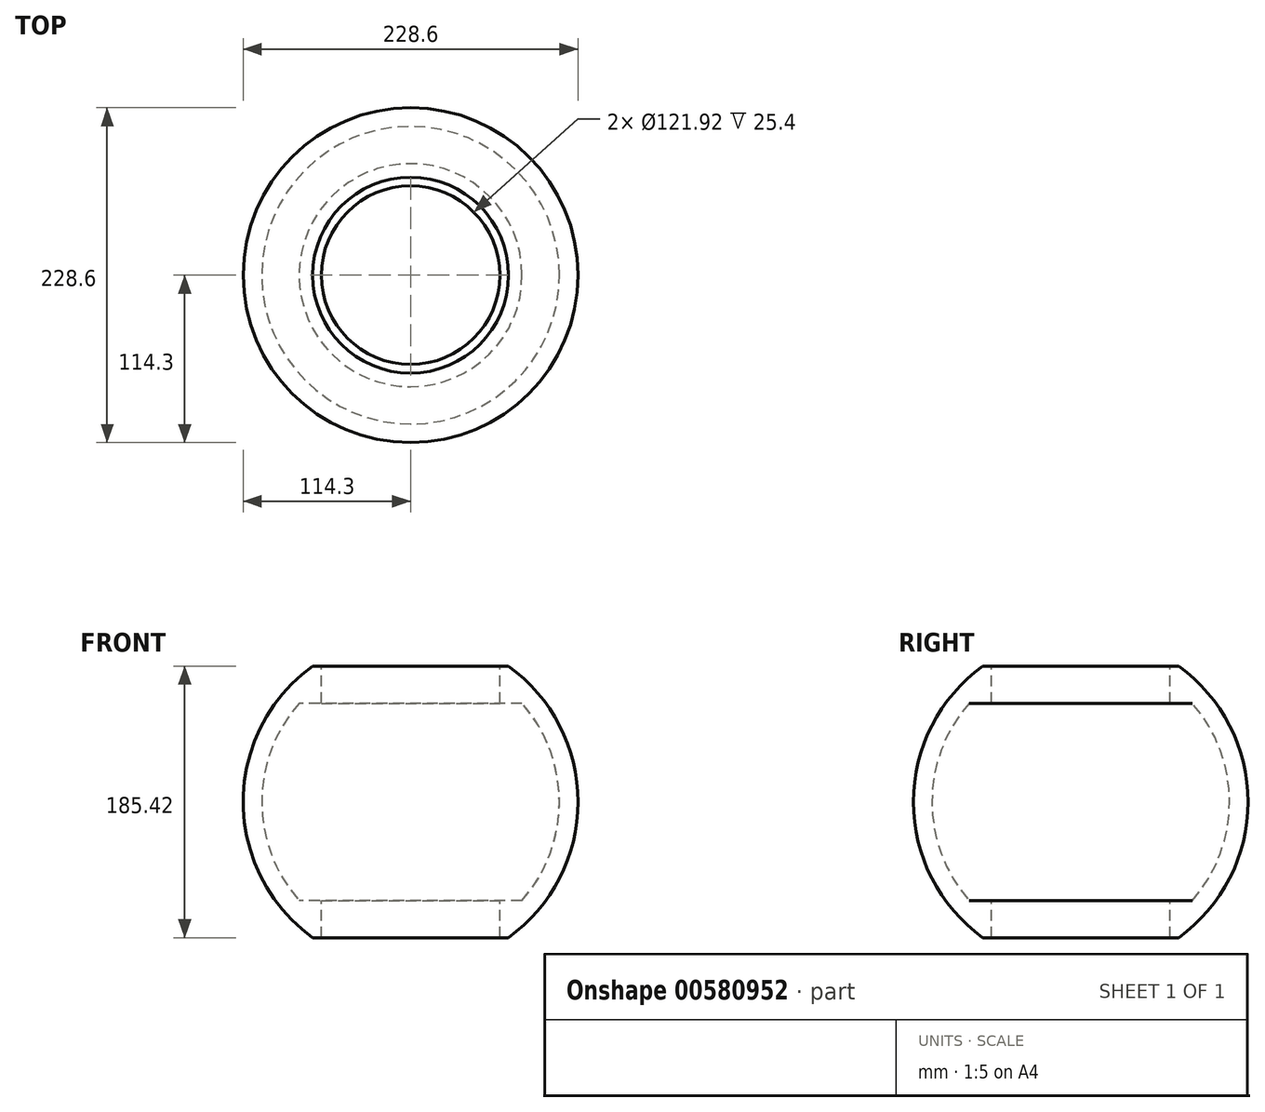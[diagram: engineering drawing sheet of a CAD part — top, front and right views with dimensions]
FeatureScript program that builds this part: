
annotation { "Feature Type Name" : "Feature", "Feature Type Description" : "" }
export const myFeature = defineFeature(function(context is Context, id is Id, definition is map)
    precondition{}
    {
        {
            var Q0;
            Q0=qCreatedBy(makeId("Front.planeOp"),FACE);
            var sketch = newSketch(context, id + "F0", { "sketchPlane" : qUnion([Q0])});
            skArc(sketch, "E0", {"start": v(0, -114.3) * mm, "mid": v(114.3, 0) * mm, "end": v(0, 114.3) * mm});
            skLineSegment(sketch, "E1", {"start": v(0, 114.3) * mm, "end": v(0, -114.3) * mm});
            skSolve(sketch);
        }
        {
            var Q0;
            Q0=makeQuery(id+"F0.imprint","IMPRINT",FACE,{"disambiguationData":[TD([[makeQuery(id+"F0.imprint","IMPRINT",EDGE,{"derivedFrom":sQuery(id+"F0.wireOp",EDGE,"E0")}),1.0]])]});
            var Q1;
            Q1=sQuery(id+"F0.wireOp",EDGE,"E0");
            var Q2;
            Q2=sQuery(id+"F0.wireOp",EDGE,"E1");
            revolve(context, id + "F1", {"entities" : qUnion([Q0]), "surfaceEntities" : qUnion([Q1]), "axis" : qUnion([Q2]), "revolveType" : RevolveType.FULL});
        }
        {
            var Q0;
            Q0=qCreatedBy(makeId("Top.planeOp"),FACE);
            var sketch = newSketch(context, id + "F2", { "sketchPlane" : qUnion([Q0])});
            skCircle(sketch, "E2", {"center": v(0, 0) * mm, "radius": 60.96 * mm});
            skSolve(sketch);
        }
        {
            var Q0;
            Q0=qSketchRegion(id+"F2",true);
            extrude(context, id + "F3", {"entities" : qUnion([Q0]), "operationType" : NewBodyOperationType.REMOVE, "endBound" : BoundingType.THROUGH_ALL, "oppositeDirection" : true, "depth" : 25.4 * mm, "offsetDistance" : 25.4 * mm, "hasSecondDirection" : true, "secondDirectionBound" : SecondDirectionBoundingType.THROUGH_ALL, "secondDirectionOppositeDirection" : false, "secondDirectionDepth" : 25.4 * mm});
        }
        {
            var Q0;
            Q0=qCreatedBy(makeId("Front.planeOp"),FACE);
            var sketch = newSketch(context, id + "F4", { "sketchPlane" : qUnion([Q0])});
            skLineSegment(sketch, "E3.bottom", {"start": v(-129.8, 129.8) * mm, "end": v(129.8, 129.8) * mm});
            skLineSegment(sketch, "E3.top", {"start": v(-129.8, 92.7) * mm, "end": v(129.8, 92.7) * mm});
            skLineSegment(sketch, "E3.left", {"start": v(-129.8, 129.8) * mm, "end": v(-129.8, 92.7) * mm});
            skLineSegment(sketch, "E3.right", {"start": v(129.8, 129.8) * mm, "end": v(129.8, 92.7) * mm});
            skLineSegment(sketch, "E4.MirrorCS", {"start": v(-129.8, -129.8) * mm, "end": v(129.8, -129.8) * mm});
            skLineSegment(sketch, "E5.MirrorCS", {"start": v(-129.8, -129.8) * mm, "end": v(-129.8, -92.7) * mm});
            skLineSegment(sketch, "E6.MirrorCS", {"start": v(-129.8, -92.7) * mm, "end": v(129.8, -92.7) * mm});
            skLineSegment(sketch, "E7.MirrorCS", {"start": v(129.8, -129.8) * mm, "end": v(129.8, -92.7) * mm});
            skSolve(sketch);
        }
        {
            var Q0;
            Q0=makeQuery(id+"F4.imprint","IMPRINT",FACE,{"disambiguationData":[TD([[makeQuery(id+"F4.imprint","IMPRINT",EDGE,{"derivedFrom":sQuery(id+"F4.wireOp",EDGE,"E3.bottom")}),-1.0]])]});
            var Q1;
            Q1=makeQuery(id+"F4.imprint","IMPRINT",FACE,{"disambiguationData":[TD([[makeQuery(id+"F4.imprint","IMPRINT",EDGE,{"derivedFrom":sQuery(id+"F4.wireOp",EDGE,"E4.MirrorCS")}),1.0]])]});
            extrude(context, id + "F5", {"entities" : qUnion([Q0, Q1]), "operationType" : NewBodyOperationType.REMOVE, "endBound" : BoundingType.THROUGH_ALL, "oppositeDirection" : true, "depth" : 25.4 * mm, "offsetDistance" : 25.4 * mm, "hasSecondDirection" : true, "secondDirectionBound" : SecondDirectionBoundingType.THROUGH_ALL, "secondDirectionOppositeDirection" : false, "secondDirectionDepth" : 25.4 * mm});
        }
        {
            var Q0;
            Q0=qCreatedBy(makeId("Right.planeOp"),FACE);
            var sketch = newSketch(context, id + "F6", { "sketchPlane" : qUnion([Q0])});
            skArc(sketch, "E8", {"start": v(-76.1, 67.3) * mm, "mid": v(-101.6, 0) * mm, "end": v(-76.1, -67.31) * mm});
            skLineSegment(sketch, "E9", {"start": v(-76.1, 67.3) * mm, "end": v(0, 67.3) * mm});
            skLineSegment(sketch, "E10", {"start": v(-76.1, -67.3) * mm, "end": v(0, -67.3) * mm});
            skLineSegment(sketch, "E11", {"start": v(0, -67.3) * mm, "end": v(0, 67.3) * mm});
            skSolve(sketch);
        }
        {
            var Q0;
            Q0 = qSketchRegion(id + "F6", true);
            var Q1;
            Q1=sQuery(id+"F6.wireOp",EDGE,"E11");
            revolve(context, id + "F7", {"operationType" : NewBodyOperationType.REMOVE, "surfaceOperationType" : NewSurfaceOperationType.NEW, "entities" : qUnion([Q0]), "axis" : qUnion([Q1]), "revolveType" : RevolveType.FULL, "oppositeDirection" : true});
        }
    });
